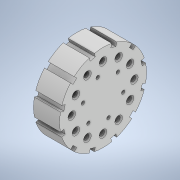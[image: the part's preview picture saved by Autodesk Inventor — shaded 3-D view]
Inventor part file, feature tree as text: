
AUTODESK INVENTOR PART (.ipt)
format: ipt  version: 2022 (Build 260153000, 153)  size: 267,264 bytes
history: native  units: mm
features: sketch x4, hole x2, chamfer x2, other x1, revolve x1, extrude x1
ambient origin geometry x8: Origin, YZ Plane, XZ Plane, XY Plane, X Axis, Y Axis, Z Axis, Center Point
bodies: Body1 (feature_tree)
feature tree (11):
  other  "Твердое тело1"
  revolve  "Вращение1"
  extrude  "Выдавливание1"  Depth=15.0mm
  hole  "Отверстие1"  [1 undecoded]
  chamfer  "Фаска1"  Angle=90.0deg  [1 undecoded]
  chamfer  "Фаска2"  Distance=3.0mm
  hole  "Отверстие2"  [1 undecoded]
  sketch  "Эскиз1"
  sketch  "Эскиз2"
  sketch  "Эскиз3"
  sketch  "Эскиз4"
note: 3 required parameter values undecoded (feature->parameter linkage not recoverable at this tier; creation-order binding heuristic only, values carry confidence <= 0.55)
